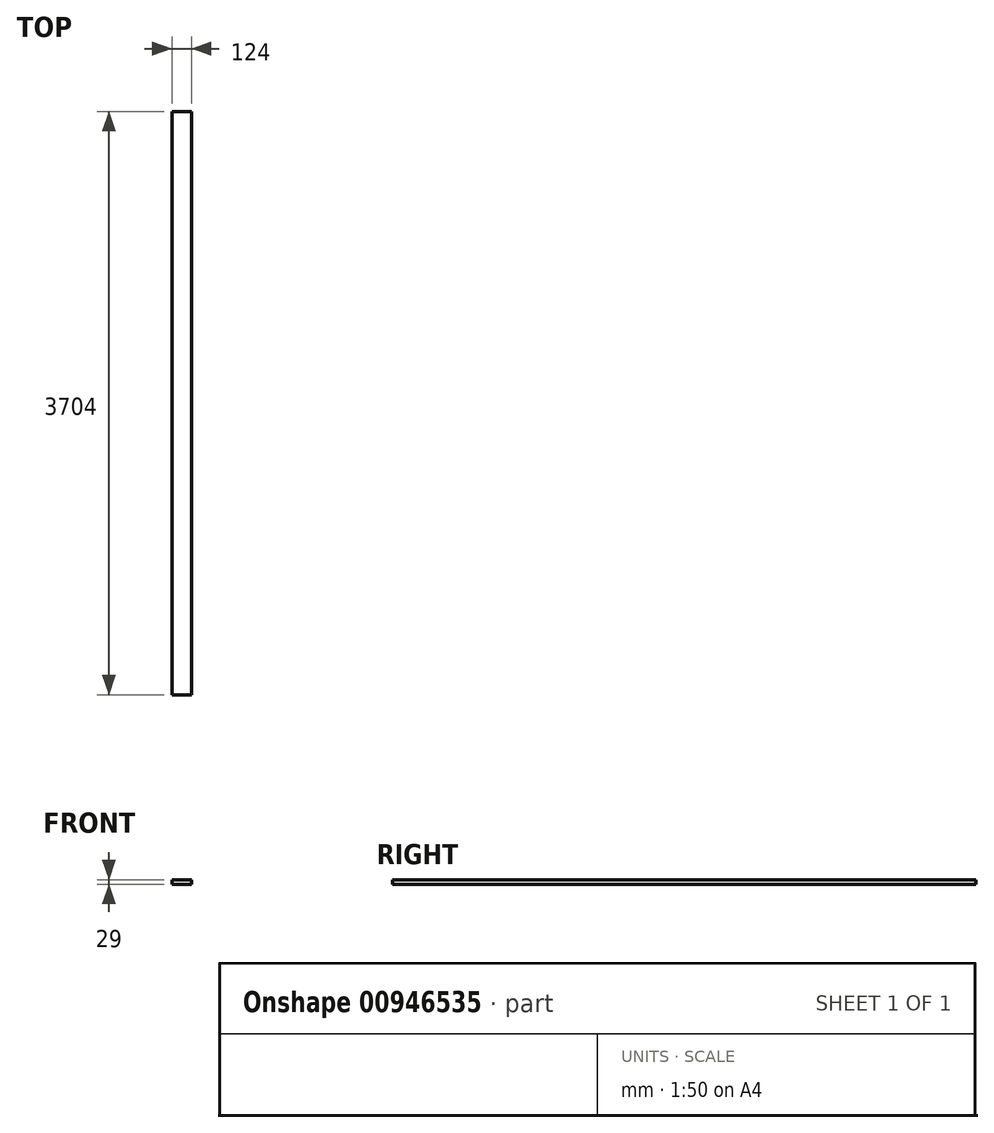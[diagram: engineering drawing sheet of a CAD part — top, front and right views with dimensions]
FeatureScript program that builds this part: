
annotation { "Feature Type Name" : "Feature", "Feature Type Description" : "" }
export const myFeature = defineFeature(function(context is Context, id is Id, definition is map)
    precondition{}
    {
        {
            var Q0;
            Q0=qCreatedBy(makeId("Front.planeOp"),FACE);
            var sketch = newSketch(context, id + "F0", { "sketchPlane" : qUnion([Q0])});
            skLineSegment(sketch, "E0.bottom", {"start": v(0, 0) * mm, "end": v(124, 0) * mm});
            skLineSegment(sketch, "E0.top", {"start": v(0, 29) * mm, "end": v(124, 29) * mm});
            skLineSegment(sketch, "E0.left", {"start": v(0, 0) * mm, "end": v(0, 29) * mm});
            skLineSegment(sketch, "E0.right", {"start": v(124, 0) * mm, "end": v(124, 29) * mm});
            skSolve(sketch);
        }
        {
            var Q0;
            Q0=qSketchRegion(id+"F0",true);
            extrude(context, id + "F1", {"entities" : qUnion([Q0]), "depth" : 3704 * mm, "offsetDistance" : 25 * mm});
        }
    });
